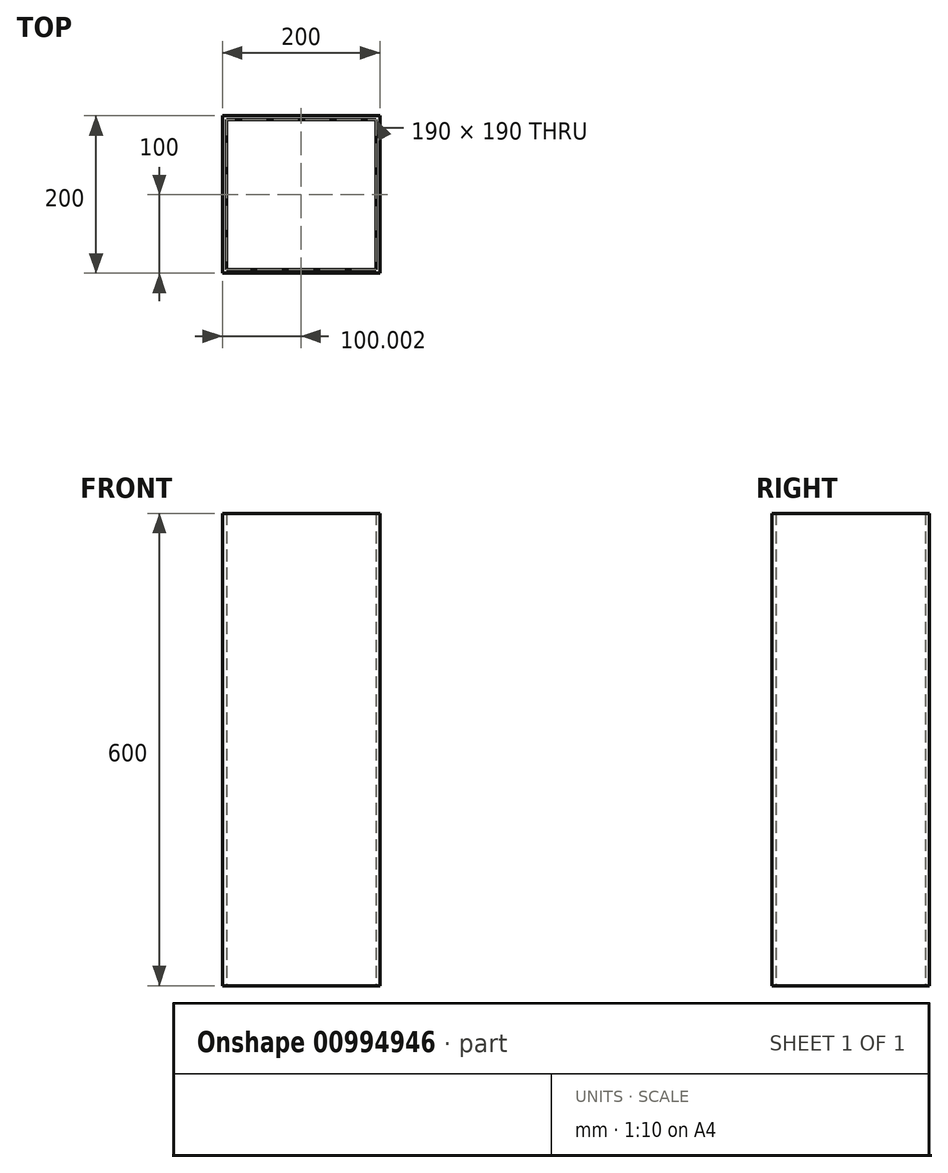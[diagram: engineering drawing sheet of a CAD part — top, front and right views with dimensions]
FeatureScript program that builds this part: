
annotation { "Feature Type Name" : "Feature", "Feature Type Description" : "" }
export const myFeature = defineFeature(function(context is Context, id is Id, definition is map)
    precondition{}
    {
        {
            var Q0;
            Q0=qCreatedBy(makeId("Top.planeOp"),FACE);
            var sketch = newSketch(context, id + "F0", { "sketchPlane" : qUnion([Q0])});
            skLineSegment(sketch, "E0.bottom", {"start": v(-148.44, 0) * mm, "end": v(-348.44, 0) * mm});
            skLineSegment(sketch, "E0.top", {"start": v(-148.44, 200) * mm, "end": v(-348.44, 200) * mm});
            skLineSegment(sketch, "E0.left", {"start": v(-148.44, 0) * mm, "end": v(-148.44, 200) * mm});
            skLineSegment(sketch, "E0.right", {"start": v(-348.44, 0) * mm, "end": v(-348.44, 200) * mm});
            skPoint(sketch, "E0.middle", {"position": v(-248.44, 100) * mm});
            skLineSegment(sketch, "E1.bottom", {"start": v(-153.44, 195) * mm, "end": v(-343.44, 195) * mm});
            skLineSegment(sketch, "E1.top", {"start": v(-153.44, 5) * mm, "end": v(-343.44, 5) * mm});
            skLineSegment(sketch, "E1.left", {"start": v(-153.44, 195) * mm, "end": v(-153.44, 5) * mm});
            skLineSegment(sketch, "E1.right", {"start": v(-343.44, 195) * mm, "end": v(-343.44, 5) * mm});
            skSolve(sketch);
        }
        {
            var Q0;
            Q0 = qSketchRegion(id + "F0", true);
            extrude(context, id + "F1", {"entities" : qUnion([Q0]), "depth" : 600 * mm, "offsetDistance" : 25 * mm});
        }
    });
